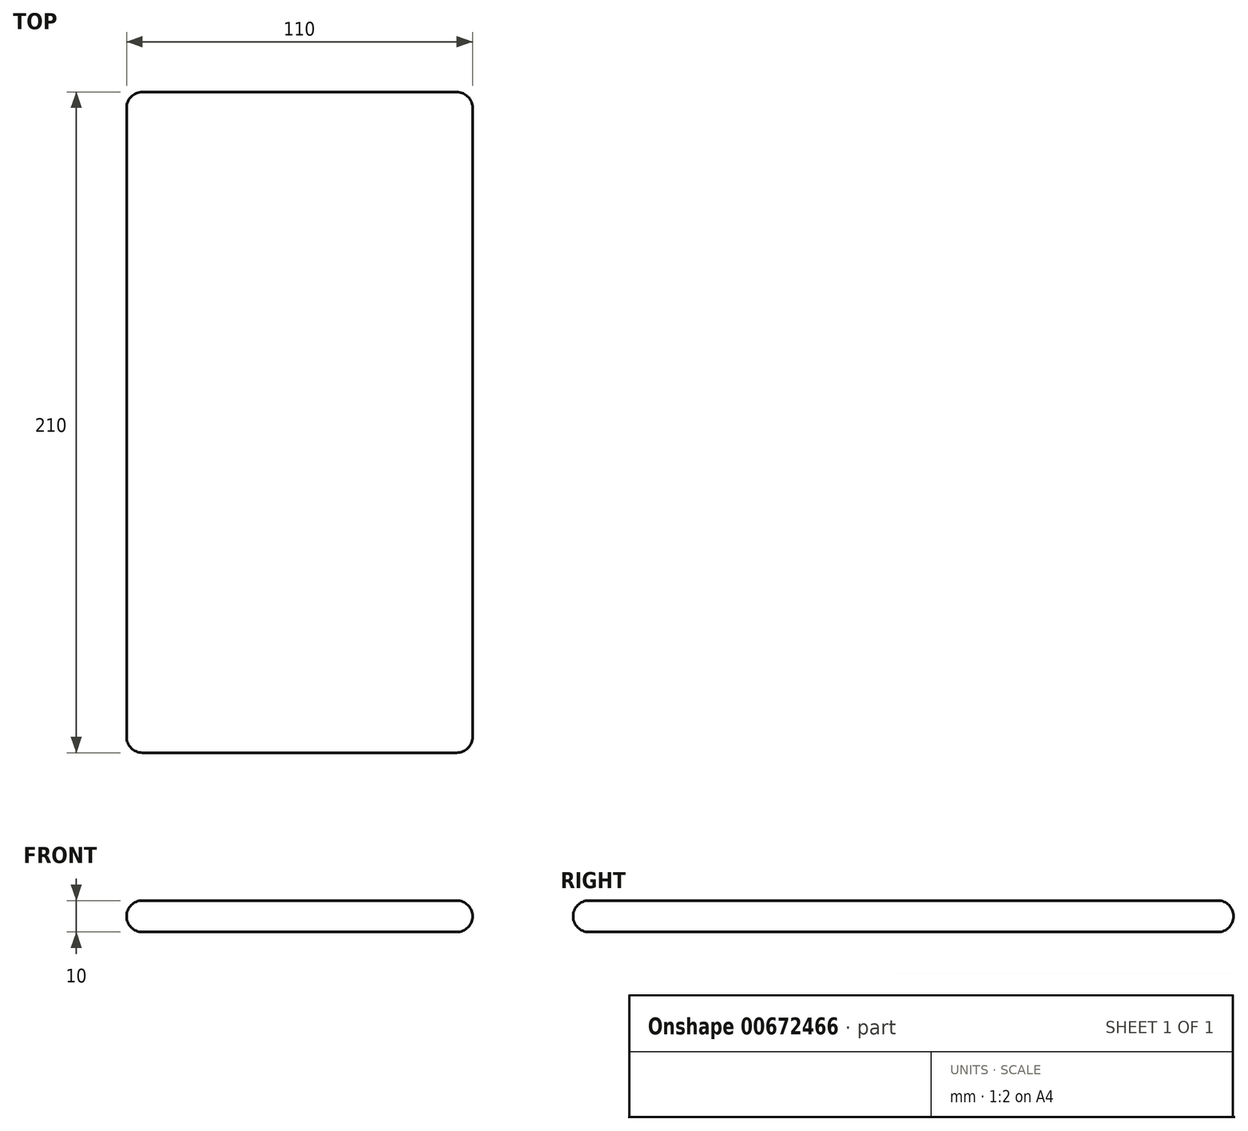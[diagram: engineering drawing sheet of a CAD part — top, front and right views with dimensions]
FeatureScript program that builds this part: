
annotation { "Feature Type Name" : "Feature", "Feature Type Description" : "" }
export const myFeature = defineFeature(function(context is Context, id is Id, definition is map)
    precondition{}
    {
        {
            var Q0;
            Q0=qCreatedBy(makeId("Top.planeOp"),FACE);
            var sketch = newSketch(context, id + "F0", { "sketchPlane" : qUnion([Q0])});
            skLineSegment(sketch, "E0.bottom", {"start": v(55, -105) * mm, "end": v(-55, -105) * mm});
            skLineSegment(sketch, "E0.top", {"start": v(55, 105) * mm, "end": v(-55, 105) * mm});
            skLineSegment(sketch, "E0.left", {"start": v(55, -105) * mm, "end": v(55, 105) * mm});
            skLineSegment(sketch, "E0.right", {"start": v(-55, -105) * mm, "end": v(-55, 105) * mm});
            skPoint(sketch, "E0.middle", {"position": v(0, 0) * mm});
            skSolve(sketch);
        }
        {
            var Q0;
            Q0 = qSketchRegion(id + "F0", true);
            extrude(context, id + "F1", {"entities" : qUnion([Q0]), "depth" : 10 * mm, "offsetDistance" : 25 * mm});
        }
        {
            var Q0;
            Q0=makeQuery(id+"F1.opExtrude","CAP_EDGE",EDGE,{"disambiguationData":[OSD([sQuery(id+"F0.wireOp",EDGE,"E0.right")])],"isStart":false});
            var Q1;
            Q1=makeQuery(id+"F1.opExtrude","CAP_EDGE",EDGE,{"disambiguationData":[OSD([sQuery(id+"F0.wireOp",EDGE,"E0.bottom")])],"isStart":false});
            var Q2;
            Q2=makeQuery(id+"F1.opExtrude","CAP_EDGE",EDGE,{"disambiguationData":[OSD([sQuery(id+"F0.wireOp",EDGE,"E0.bottom")])],"isStart":true});
            var Q3;
            Q3=makeQuery(id+"F1.opExtrude","SWEPT_EDGE",EDGE,{"disambiguationData":[OSD([sQuery(id+"F0.wireOp",EDGE,"E0.bottom"),sQuery(id+"F0.wireOp",EDGE,"E0.right")])]});
            var Q4;
            Q4=makeQuery(id+"F1.opExtrude","CAP_EDGE",EDGE,{"disambiguationData":[OSD([sQuery(id+"F0.wireOp",EDGE,"E0.right")])],"isStart":true});
            var Q5;
            Q5=makeQuery(id+"F1.opExtrude","SWEPT_EDGE",EDGE,{"disambiguationData":[OSD([sQuery(id+"F0.wireOp",EDGE,"E0.top"),sQuery(id+"F0.wireOp",EDGE,"E0.right")])]});
            var Q6;
            Q6=makeQuery(id+"F1.opExtrude","CAP_EDGE",EDGE,{"disambiguationData":[OSD([sQuery(id+"F0.wireOp",EDGE,"E0.top")])],"isStart":false});
            var Q7;
            Q7=makeQuery(id+"F1.opExtrude","CAP_EDGE",EDGE,{"disambiguationData":[OSD([sQuery(id+"F0.wireOp",EDGE,"E0.top")])],"isStart":true});
            var Q8;
            Q8=makeQuery(id+"F1.opExtrude","SWEPT_EDGE",EDGE,{"disambiguationData":[OSD([sQuery(id+"F0.wireOp",EDGE,"E0.top"),sQuery(id+"F0.wireOp",EDGE,"E0.left")])]});
            var Q9;
            Q9=makeQuery(id+"F1.opExtrude","CAP_EDGE",EDGE,{"disambiguationData":[OSD([sQuery(id+"F0.wireOp",EDGE,"E0.left")])],"isStart":false});
            var Q10;
            Q10=makeQuery(id+"F1.opExtrude","CAP_EDGE",EDGE,{"disambiguationData":[OSD([sQuery(id+"F0.wireOp",EDGE,"E0.left")])],"isStart":true});
            var Q11;
            Q11=makeQuery(id+"F1.opExtrude","SWEPT_EDGE",EDGE,{"disambiguationData":[OSD([sQuery(id+"F0.wireOp",EDGE,"E0.bottom"),sQuery(id+"F0.wireOp",EDGE,"E0.left")])]});
            fillet(context, id + "F2", {"entities" : qUnion([Q0, Q1, Q2, Q3, Q4, Q5, Q6, Q7, Q8, Q9, Q10, Q11]), "radius" : 5 * mm, "tangentPropagation" : true, "allowEdgeOverflow" : false});
        }
    });
